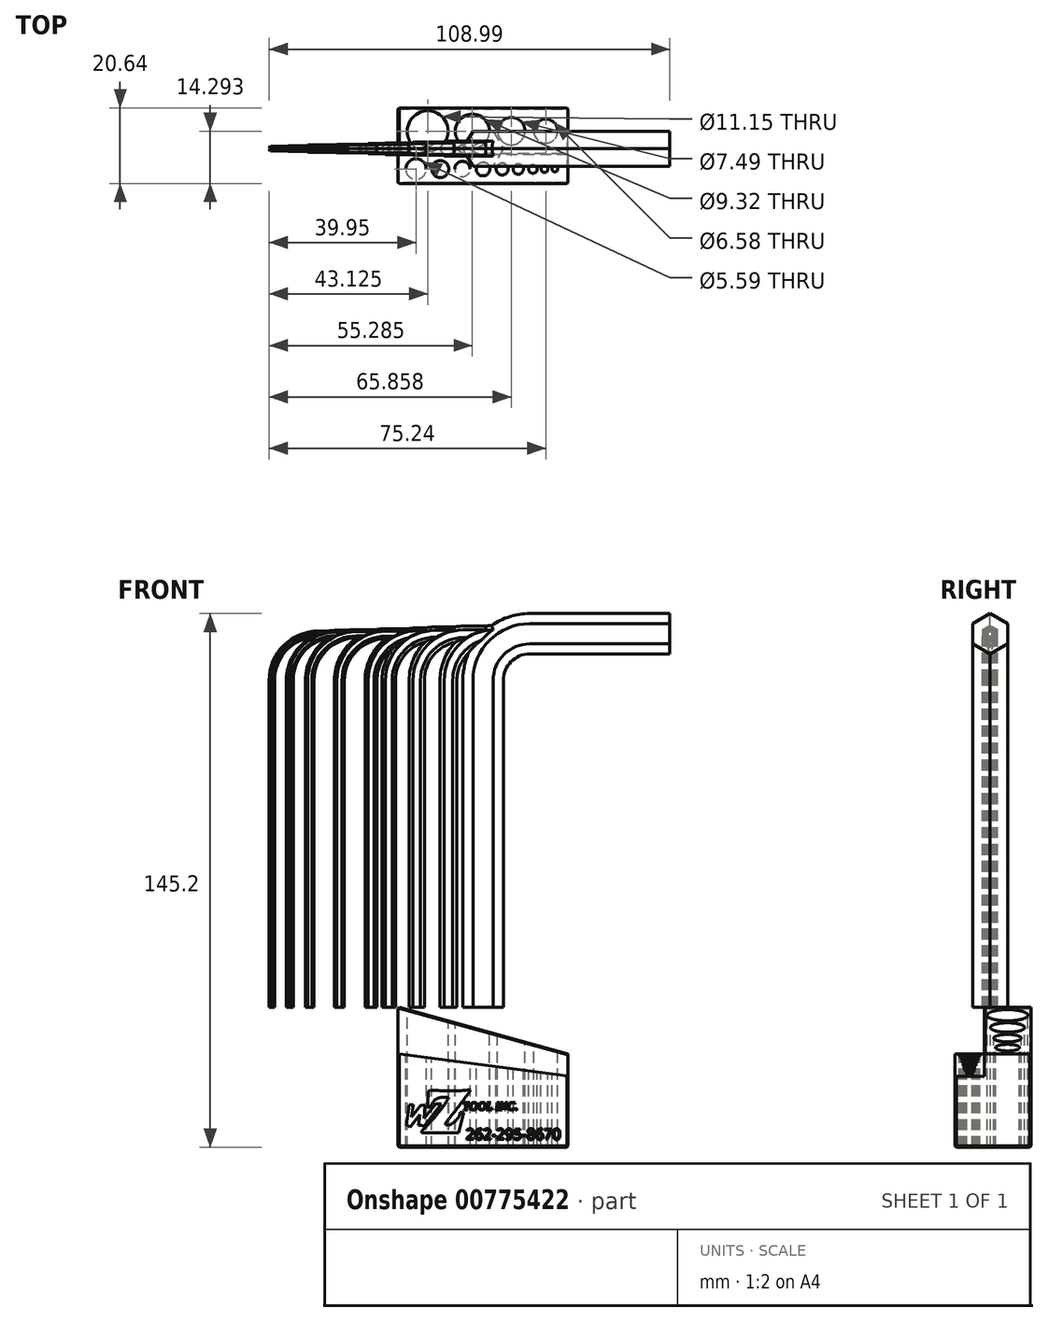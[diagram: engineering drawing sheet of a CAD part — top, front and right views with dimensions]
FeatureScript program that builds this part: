
annotation { "Feature Type Name" : "Feature", "Feature Type Description" : "" }
export const myFeature = defineFeature(function(context is Context, id is Id, definition is map)
    precondition{}
    {
        {
            var Q0;
            Q0=qCreatedBy(makeId("Top.planeOp"),FACE);
            var sketch = newSketch(context, id + "F0", { "sketchPlane" : qUnion([Q0])});
            skCircle(sketch, "E0.cCircle", {"center": v(0, 0) * mm, "radius": 4.76 * mm, "construction": true});
            skLineSegment(sketch, "E0.0", {"start": v(5.5, 0) * mm, "end": v(2.75, -4.76) * mm});
            skLineSegment(sketch, "E0.1", {"start": v(2.75, -4.76) * mm, "end": v(-2.75, -4.76) * mm});
            skLineSegment(sketch, "E0.2", {"start": v(-2.75, -4.76) * mm, "end": v(-5.5, 0) * mm});
            skLineSegment(sketch, "E0.3", {"start": v(-5.5, 0) * mm, "end": v(-2.75, 4.76) * mm});
            skLineSegment(sketch, "E0.4", {"start": v(-2.75, 4.76) * mm, "end": v(2.75, 4.76) * mm});
            skLineSegment(sketch, "E0.5", {"start": v(2.75, 4.76) * mm, "end": v(5.5, 0) * mm});
            skSolve(sketch);
        }
        {
            var Q0;
            Q0=qCreatedBy(makeId("Front.planeOp"),FACE);
            var sketch = newSketch(context, id + "F1", { "sketchPlane" : qUnion([Q0])});
            skPoint(sketch, "E1.0", {"position": v(0, 0) * mm});
            skLineSegment(sketch, "E2", {"start": v(0, 0) * mm, "end": v(0, 88.9) * mm});
            skLineSegment(sketch, "E3", {"start": v(12.7, 101.6) * mm, "end": v(50.8, 101.6) * mm});
            skPoint(sketch, "E4.visualSharp", {"position": v(0, 101.6) * mm});
            skArc(sketch, "E4.filletArc", {"start": v(12.7, 101.6) * mm, "mid": v(3.72, 97.88) * mm, "end": v(0, 88.9) * mm});
            skSolve(sketch);
        }
        {
            var Q0;
            Q0=makeQuery(id+"F0.imprint","IMPRINT",FACE,{"disambiguationData":[TD([[makeQuery(id+"F0.imprint","IMPRINT",EDGE,{"derivedFrom":sQuery(id+"F0.wireOp",EDGE,"E0.0")}),-1.0]])]});
            var Q1;
            Q1=sQuery(id+"F1.wireOp",EDGE,"E2");
            var Q2;
            Q2=sQuery(id+"F1.wireOp",EDGE,"E4.filletArc");
            var Q3;
            Q3=sQuery(id+"F1.wireOp",EDGE,"E3");
            sweep(context, id + "F2", {"profiles" : qUnion([Q0]), "path" : qUnion([Q1, Q2, Q3])});
        }
        {
            var Q0;
            Q0=qCreatedBy(makeId("Top.planeOp"),FACE);
            var sketch = newSketch(context, id + "F3", { "sketchPlane" : qUnion([Q0])});
            skCircle(sketch, "E5.cCircle", {"center": v(0, 0) * mm, "radius": 3.97 * mm, "construction": true});
            skLineSegment(sketch, "E5.0", {"start": v(4.58, 0) * mm, "end": v(2.3, -3.97) * mm});
            skLineSegment(sketch, "E5.1", {"start": v(2.3, -3.97) * mm, "end": v(-2.3, -3.97) * mm});
            skLineSegment(sketch, "E5.2", {"start": v(-2.3, -3.97) * mm, "end": v(-4.58, 0) * mm});
            skLineSegment(sketch, "E5.3", {"start": v(-4.58, 0) * mm, "end": v(-2.3, 3.97) * mm});
            skLineSegment(sketch, "E5.4", {"start": v(-2.3, 3.97) * mm, "end": v(2.3, 3.97) * mm});
            skLineSegment(sketch, "E5.5", {"start": v(2.3, 3.97) * mm, "end": v(4.58, 0) * mm});
            skSolve(sketch);
        }
        {
            var Q0;
            Q0 = qSketchRegion(id + "F3", true);
            var Q1;
            Q1=sQuery(id+"F1.wireOp",EDGE,"E2");
            var Q2;
            Q2=sQuery(id+"F1.wireOp",EDGE,"E4.filletArc");
            var Q3;
            Q3=sQuery(id+"F1.wireOp",EDGE,"E3");
            sweep(context, id + "F4", {"profiles" : qUnion([Q0]), "path" : qUnion([Q1, Q2, Q3])});
        }
        {
            var Q0;
            Q0=qCreatedBy(makeId("Top.planeOp"),FACE);
            var sketch = newSketch(context, id + "F5", { "sketchPlane" : qUnion([Q0])});
            skCircle(sketch, "E6.cCircle", {"center": v(0, 0) * mm, "radius": 3.18 * mm, "construction": true});
            skLineSegment(sketch, "E6.0", {"start": v(3.67, 0) * mm, "end": v(1.83, -3.17) * mm});
            skLineSegment(sketch, "E6.1", {"start": v(1.83, -3.17) * mm, "end": v(-1.83, -3.17) * mm});
            skLineSegment(sketch, "E6.2", {"start": v(-1.83, -3.17) * mm, "end": v(-3.67, 0) * mm});
            skLineSegment(sketch, "E6.3", {"start": v(-3.67, 0) * mm, "end": v(-1.83, 3.17) * mm});
            skLineSegment(sketch, "E6.4", {"start": v(-1.83, 3.17) * mm, "end": v(1.83, 3.17) * mm});
            skLineSegment(sketch, "E6.5", {"start": v(1.83, 3.17) * mm, "end": v(3.67, 0) * mm});
            skSolve(sketch);
        }
        {
            var Q0;
            Q0 = qSketchRegion(id + "F5", true);
            var Q1;
            Q1=sQuery(id+"F1.wireOp",EDGE,"E2");
            var Q2;
            Q2=sQuery(id+"F1.wireOp",EDGE,"E4.filletArc");
            var Q3;
            Q3=sQuery(id+"F1.wireOp",EDGE,"E3");
            sweep(context, id + "F6", {"profiles" : qUnion([Q0]), "path" : qUnion([Q1, Q2, Q3])});
        }
        {
            var Q0;
            Q0=qCreatedBy(makeId("Top.planeOp"),FACE);
            var sketch = newSketch(context, id + "F7", { "sketchPlane" : qUnion([Q0])});
            skCircle(sketch, "E7.cCircle", {"center": v(0, 0) * mm, "radius": 2.78 * mm, "construction": true});
            skLineSegment(sketch, "E7.0", {"start": v(3.2, 0) * mm, "end": v(1.6, -2.78) * mm});
            skLineSegment(sketch, "E7.1", {"start": v(1.6, -2.78) * mm, "end": v(-1.6, -2.78) * mm});
            skLineSegment(sketch, "E7.2", {"start": v(-1.6, -2.78) * mm, "end": v(-3.2, 0) * mm});
            skLineSegment(sketch, "E7.3", {"start": v(-3.2, 0) * mm, "end": v(-1.6, 2.78) * mm});
            skLineSegment(sketch, "E7.4", {"start": v(-1.6, 2.78) * mm, "end": v(1.6, 2.78) * mm});
            skLineSegment(sketch, "E7.5", {"start": v(1.6, 2.78) * mm, "end": v(3.2, 0) * mm});
            skSolve(sketch);
        }
        {
            var Q0;
            Q0=makeQuery(id+"F7.imprint","IMPRINT",FACE,{"disambiguationData":[TD([[makeQuery(id+"F7.imprint","IMPRINT",EDGE,{"derivedFrom":sQuery(id+"F7.wireOp",EDGE,"E7.0")}),-1.0]])]});
            var Q1;
            Q1=sQuery(id+"F1.wireOp",EDGE,"E2");
            var Q2;
            Q2=sQuery(id+"F1.wireOp",EDGE,"E4.filletArc");
            var Q3;
            Q3=sQuery(id+"F1.wireOp",EDGE,"E3");
            sweep(context, id + "F8", {"profiles" : qUnion([Q0]), "path" : qUnion([Q1, Q2, Q3])});
        }
        {
            var Q0;
            Q0=qCreatedBy(makeId("Top.planeOp"),FACE);
            var sketch = newSketch(context, id + "F9", { "sketchPlane" : qUnion([Q0])});
            skCircle(sketch, "E8.cCircle", {"center": v(0, 0) * mm, "radius": 2.38 * mm, "construction": true});
            skLineSegment(sketch, "E8.0", {"start": v(2.75, 0) * mm, "end": v(1.37, -2.38) * mm});
            skLineSegment(sketch, "E8.1", {"start": v(1.37, -2.38) * mm, "end": v(-1.37, -2.38) * mm});
            skLineSegment(sketch, "E8.2", {"start": v(-1.37, -2.38) * mm, "end": v(-2.75, 0) * mm});
            skLineSegment(sketch, "E8.3", {"start": v(-2.75, 0) * mm, "end": v(-1.37, 2.38) * mm});
            skLineSegment(sketch, "E8.4", {"start": v(-1.37, 2.38) * mm, "end": v(1.37, 2.38) * mm});
            skLineSegment(sketch, "E8.5", {"start": v(1.37, 2.38) * mm, "end": v(2.75, 0) * mm});
            skSolve(sketch);
        }
        {
            var Q0;
            Q0 = qSketchRegion(id + "F9", true);
            var Q1;
            Q1=sQuery(id+"F1.wireOp",EDGE,"E2");
            var Q2;
            Q2=sQuery(id+"F1.wireOp",EDGE,"E4.filletArc");
            var Q3;
            Q3=sQuery(id+"F1.wireOp",EDGE,"E3");
            sweep(context, id + "F10", {"profiles" : qUnion([Q0]), "path" : qUnion([Q1, Q2, Q3])});
        }
        {
            var Q0;
            Q0=qCreatedBy(makeId("Top.planeOp"),FACE);
            var sketch = newSketch(context, id + "F11", { "sketchPlane" : qUnion([Q0])});
            skCircle(sketch, "E9.cCircle", {"center": v(-47.15, 0) * mm, "radius": 1 * mm, "construction": true});
            skLineSegment(sketch, "E9.0", {"start": v(-46, 0) * mm, "end": v(-46.58, -1) * mm});
            skLineSegment(sketch, "E9.1", {"start": v(-46.58, -1) * mm, "end": v(-47.72, -1) * mm});
            skLineSegment(sketch, "E9.2", {"start": v(-47.72, -1) * mm, "end": v(-48.3, 0) * mm});
            skLineSegment(sketch, "E9.3", {"start": v(-48.3, 0) * mm, "end": v(-47.72, 1) * mm});
            skLineSegment(sketch, "E9.4", {"start": v(-47.72, 1) * mm, "end": v(-46.58, 1) * mm});
            skLineSegment(sketch, "E9.5", {"start": v(-46.58, 1) * mm, "end": v(-46, 0) * mm});
            skCircle(sketch, "E10.cCircle", {"center": v(-39.07, 0) * mm, "radius": 1.2 * mm, "construction": true});
            skLineSegment(sketch, "E10.0", {"start": v(-37.7, 0) * mm, "end": v(-38.39, -1.2) * mm});
            skLineSegment(sketch, "E10.1", {"start": v(-38.39, -1.2) * mm, "end": v(-39.76, -1.2) * mm});
            skLineSegment(sketch, "E10.2", {"start": v(-39.76, -1.2) * mm, "end": v(-40.45, 0) * mm});
            skLineSegment(sketch, "E10.3", {"start": v(-40.45, 0) * mm, "end": v(-39.76, 1.2) * mm});
            skLineSegment(sketch, "E10.4", {"start": v(-39.76, 1.2) * mm, "end": v(-38.39, 1.2) * mm});
            skLineSegment(sketch, "E10.5", {"start": v(-38.39, 1.2) * mm, "end": v(-37.7, 0) * mm});
            skCircle(sketch, "E11.cCircle", {"center": v(-52.58, 0) * mm, "radius": 0.8 * mm, "construction": true});
            skLineSegment(sketch, "E11.0", {"start": v(-51.66, 0) * mm, "end": v(-52.12, -0.8) * mm});
            skLineSegment(sketch, "E11.1", {"start": v(-52.12, -0.8) * mm, "end": v(-53.04, -0.8) * mm});
            skLineSegment(sketch, "E11.2", {"start": v(-53.04, -0.8) * mm, "end": v(-53.5, 0) * mm});
            skLineSegment(sketch, "E11.3", {"start": v(-53.5, 0) * mm, "end": v(-53.04, 0.8) * mm});
            skLineSegment(sketch, "E11.4", {"start": v(-53.04, 0.8) * mm, "end": v(-52.12, 0.8) * mm});
            skLineSegment(sketch, "E11.5", {"start": v(-52.12, 0.8) * mm, "end": v(-51.66, 0) * mm});
            skCircle(sketch, "E12.cCircle", {"center": v(-57.46, 0) * mm, "radius": 0.64 * mm, "construction": true});
            skLineSegment(sketch, "E12.0", {"start": v(-56.73, 0) * mm, "end": v(-57.1, -0.64) * mm});
            skLineSegment(sketch, "E12.1", {"start": v(-57.1, -0.63) * mm, "end": v(-57.83, -0.64) * mm});
            skLineSegment(sketch, "E12.2", {"start": v(-57.83, -0.63) * mm, "end": v(-58.2, 0) * mm});
            skLineSegment(sketch, "E12.3", {"start": v(-58.2, 0) * mm, "end": v(-57.83, 0.63) * mm});
            skLineSegment(sketch, "E12.4", {"start": v(-57.83, 0.63) * mm, "end": v(-57.1, 0.64) * mm});
            skLineSegment(sketch, "E12.5", {"start": v(-57.1, 0.64) * mm, "end": v(-56.73, 0) * mm});
            skCircle(sketch, "E13.cCircle", {"center": v(-9.42, 0) * mm, "radius": 1.98 * mm, "construction": true});
            skLineSegment(sketch, "E13.0", {"start": v(-7.12, 0) * mm, "end": v(-8.27, -1.98) * mm});
            skLineSegment(sketch, "E13.1", {"start": v(-8.27, -1.98) * mm, "end": v(-10.56, -1.98) * mm});
            skLineSegment(sketch, "E13.2", {"start": v(-10.56, -1.98) * mm, "end": v(-11.7, 0) * mm});
            skLineSegment(sketch, "E13.3", {"start": v(-11.7, 0) * mm, "end": v(-10.56, 1.98) * mm});
            skLineSegment(sketch, "E13.4", {"start": v(-10.56, 1.98) * mm, "end": v(-8.27, 1.98) * mm});
            skLineSegment(sketch, "E13.5", {"start": v(-8.27, 1.98) * mm, "end": v(-7.12, 0) * mm});
            skCircle(sketch, "E14.cCircle", {"center": v(-18.03, 0) * mm, "radius": 1.79 * mm, "construction": true});
            skLineSegment(sketch, "E14.0", {"start": v(-15.97, 0) * mm, "end": v(-17, -1.79) * mm});
            skLineSegment(sketch, "E14.1", {"start": v(-17, -1.79) * mm, "end": v(-19.07, -1.79) * mm});
            skLineSegment(sketch, "E14.2", {"start": v(-19.07, -1.79) * mm, "end": v(-20.1, 0) * mm});
            skLineSegment(sketch, "E14.3", {"start": v(-20.1, 0) * mm, "end": v(-19.07, 1.79) * mm});
            skLineSegment(sketch, "E14.4", {"start": v(-19.07, 1.79) * mm, "end": v(-17, 1.79) * mm});
            skLineSegment(sketch, "E14.5", {"start": v(-17, 1.79) * mm, "end": v(-15.97, 0) * mm});
            skCircle(sketch, "E15.cCircle", {"center": v(-25.65, 0) * mm, "radius": 1.59 * mm, "construction": true});
            skLineSegment(sketch, "E15.0", {"start": v(-23.82, 0) * mm, "end": v(-24.74, -1.59) * mm});
            skLineSegment(sketch, "E15.1", {"start": v(-24.74, -1.59) * mm, "end": v(-26.57, -1.59) * mm});
            skLineSegment(sketch, "E15.2", {"start": v(-26.57, -1.59) * mm, "end": v(-27.49, 0) * mm});
            skLineSegment(sketch, "E15.3", {"start": v(-27.49, 0) * mm, "end": v(-26.57, 1.59) * mm});
            skLineSegment(sketch, "E15.4", {"start": v(-26.57, 1.59) * mm, "end": v(-24.74, 1.59) * mm});
            skLineSegment(sketch, "E15.5", {"start": v(-24.74, 1.59) * mm, "end": v(-23.82, 0) * mm});
            skCircle(sketch, "E16.cCircle", {"center": v(-30.47, 0) * mm, "radius": 1.39 * mm, "construction": true});
            skLineSegment(sketch, "E16.0", {"start": v(-28.87, 0) * mm, "end": v(-29.67, -1.39) * mm});
            skLineSegment(sketch, "E16.1", {"start": v(-29.67, -1.39) * mm, "end": v(-31.28, -1.39) * mm});
            skLineSegment(sketch, "E16.2", {"start": v(-31.28, -1.39) * mm, "end": v(-32.08, 0) * mm});
            skLineSegment(sketch, "E16.3", {"start": v(-32.08, 0) * mm, "end": v(-31.28, 1.39) * mm});
            skLineSegment(sketch, "E16.4", {"start": v(-31.28, 1.39) * mm, "end": v(-29.67, 1.39) * mm});
            skLineSegment(sketch, "E16.5", {"start": v(-29.67, 1.39) * mm, "end": v(-28.87, 0) * mm});
            skSolve(sketch);
        }
        {
            var Q0;
            Q0=qCreatedBy(makeId("Front.planeOp"),FACE);
            var sketch = newSketch(context, id + "F12", { "sketchPlane" : qUnion([Q0])});
            skPoint(sketch, "E17.0", {"position": v(-9.42, 0) * mm});
            skLineSegment(sketch, "E18", {"start": v(-9.42, 0) * mm, "end": v(-9.42, 88.9) * mm});
            skLineSegment(sketch, "E19", {"start": v(3.28, 101.6) * mm, "end": v(41.38, 101.6) * mm});
            skPoint(sketch, "E20.visualSharp", {"position": v(-9.42, 101.6) * mm});
            skArc(sketch, "E20.filletArc", {"start": v(3.28, 101.6) * mm, "mid": v(-5.7, 97.88) * mm, "end": v(-9.42, 88.9) * mm});
            skPoint(sketch, "E21.0", {"position": v(-57.46, 0) * mm});
            skPoint(sketch, "E22.0", {"position": v(-52.58, 0) * mm});
            skPoint(sketch, "E23.0", {"position": v(-47.15, 0) * mm});
            skPoint(sketch, "E24.0", {"position": v(-39.07, 0) * mm});
            skPoint(sketch, "E25.0", {"position": v(-30.47, 0) * mm});
            skPoint(sketch, "E26.0", {"position": v(-25.65, 0) * mm});
            skPoint(sketch, "E27.0", {"position": v(-18.03, 0) * mm});
            skLineSegment(sketch, "E28", {"start": v(-18.03, 0) * mm, "end": v(-18.03, 88.9) * mm});
            skLineSegment(sketch, "E29", {"start": v(-5.33, 101.6) * mm, "end": v(32.77, 101.6) * mm});
            skPoint(sketch, "E30.visualSharp", {"position": v(-18.03, 101.6) * mm});
            skArc(sketch, "E30.filletArc", {"start": v(-5.33, 101.6) * mm, "mid": v(-14.31, 97.88) * mm, "end": v(-18.03, 88.9) * mm});
            skLineSegment(sketch, "E31", {"start": v(-25.65, 0) * mm, "end": v(-25.65, 88.9) * mm});
            skLineSegment(sketch, "E32", {"start": v(-12.95, 101.6) * mm, "end": v(25.15, 101.6) * mm});
            skPoint(sketch, "E33.visualSharp", {"position": v(-25.65, 101.6) * mm});
            skArc(sketch, "E33.filletArc", {"start": v(-12.95, 101.6) * mm, "mid": v(-21.93, 97.88) * mm, "end": v(-25.65, 88.9) * mm});
            skLineSegment(sketch, "E34", {"start": v(-39.07, 0) * mm, "end": v(-39.07, 88.9) * mm});
            skLineSegment(sketch, "E35", {"start": v(-26.37, 101.6) * mm, "end": v(11.73, 101.6) * mm});
            skPoint(sketch, "E36.visualSharp", {"position": v(-39.07, 101.6) * mm});
            skArc(sketch, "E36.filletArc", {"start": v(-26.37, 101.6) * mm, "mid": v(-35.35, 97.88) * mm, "end": v(-39.07, 88.9) * mm});
            skLineSegment(sketch, "E37", {"start": v(-47.15, 0) * mm, "end": v(-47.15, 88.9) * mm});
            skLineSegment(sketch, "E38", {"start": v(-34.45, 101.6) * mm, "end": v(3.65, 101.6) * mm});
            skPoint(sketch, "E39.visualSharp", {"position": v(-47.15, 101.6) * mm});
            skArc(sketch, "E39.filletArc", {"start": v(-34.45, 101.6) * mm, "mid": v(-43.43, 97.88) * mm, "end": v(-47.15, 88.9) * mm});
            skLineSegment(sketch, "E40", {"start": v(-52.58, 0) * mm, "end": v(-52.58, 88.9) * mm});
            skLineSegment(sketch, "E41", {"start": v(-39.88, 101.6) * mm, "end": v(-1.78, 101.6) * mm});
            skPoint(sketch, "E42.visualSharp", {"position": v(-52.58, 101.6) * mm});
            skArc(sketch, "E42.filletArc", {"start": v(-39.88, 101.6) * mm, "mid": v(-48.86, 97.88) * mm, "end": v(-52.58, 88.9) * mm});
            skLineSegment(sketch, "E43", {"start": v(-57.46, 0) * mm, "end": v(-57.46, 88.9) * mm});
            skLineSegment(sketch, "E44", {"start": v(-44.76, 101.6) * mm, "end": v(-6.66, 101.6) * mm});
            skPoint(sketch, "E45.visualSharp", {"position": v(-57.46, 101.6) * mm});
            skArc(sketch, "E45.filletArc", {"start": v(-44.76, 101.6) * mm, "mid": v(-53.74, 97.88) * mm, "end": v(-57.46, 88.9) * mm});
            skLineSegment(sketch, "E46", {"start": v(-30.47, 0) * mm, "end": v(-30.47, 88.9) * mm});
            skLineSegment(sketch, "E47", {"start": v(-17.77, 101.6) * mm, "end": v(20.33, 101.6) * mm});
            skPoint(sketch, "E48.visualSharp", {"position": v(-30.47, 101.6) * mm});
            skArc(sketch, "E48.filletArc", {"start": v(-17.77, 101.6) * mm, "mid": v(-26.75, 97.88) * mm, "end": v(-30.47, 88.9) * mm});
            skLineSegment(sketch, "E49", {"start": v(-12.95, 101.6) * mm, "end": v(11.73, 101.6) * mm});
            skSolve(sketch);
        }
        {
            var Q0;
            Q0=makeQuery(id+"F11.imprint","IMPRINT",FACE,{"disambiguationData":[TD([[makeQuery(id+"F11.imprint","IMPRINT",EDGE,{"derivedFrom":sQuery(id+"F11.wireOp",EDGE,"E13.0")}),-1.0]])]});
            var Q1;
            Q1=makeQuery(id+"F11.imprint","IMPRINT",FACE,{"disambiguationData":[TD([[makeQuery(id+"F11.imprint","IMPRINT",EDGE,{"derivedFrom":sQuery(id+"F11.wireOp",EDGE,"E14.0")}),-1.0]])]});
            var Q2;
            Q2=makeQuery(id+"F11.imprint","IMPRINT",FACE,{"disambiguationData":[TD([[makeQuery(id+"F11.imprint","IMPRINT",EDGE,{"derivedFrom":sQuery(id+"F11.wireOp",EDGE,"E15.0")}),-1.0]])]});
            var Q3;
            Q3=makeQuery(id+"F11.imprint","IMPRINT",FACE,{"disambiguationData":[TD([[makeQuery(id+"F11.imprint","IMPRINT",EDGE,{"derivedFrom":sQuery(id+"F11.wireOp",EDGE,"E16.0")}),-1.0]])]});
            var Q4;
            Q4=makeQuery(id+"F11.imprint","IMPRINT",FACE,{"disambiguationData":[TD([[makeQuery(id+"F11.imprint","IMPRINT",EDGE,{"derivedFrom":sQuery(id+"F11.wireOp",EDGE,"E10.0")}),-1.0]])]});
            var Q5;
            Q5=makeQuery(id+"F11.imprint","IMPRINT",FACE,{"disambiguationData":[TD([[makeQuery(id+"F11.imprint","IMPRINT",EDGE,{"derivedFrom":sQuery(id+"F11.wireOp",EDGE,"E9.0")}),-1.0]])]});
            var Q6;
            Q6=makeQuery(id+"F11.imprint","IMPRINT",FACE,{"disambiguationData":[TD([[makeQuery(id+"F11.imprint","IMPRINT",EDGE,{"derivedFrom":sQuery(id+"F11.wireOp",EDGE,"E11.0")}),-1.0]])]});
            var Q7;
            Q7=makeQuery(id+"F11.imprint","IMPRINT",FACE,{"disambiguationData":[TD([[makeQuery(id+"F11.imprint","IMPRINT",EDGE,{"derivedFrom":sQuery(id+"F11.wireOp",EDGE,"E12.0")}),-1.0]])]});
            var Q8;
            Q8=sQuery(id+"F12.wireOp",EDGE,"E18");
            sweep(context, id + "F13", {"profiles" : qUnion([Q0, Q1, Q2, Q3, Q4, Q5, Q6, Q7]), "path" : qUnion([Q8])});
        }
        {
            var Q0;
            Q0=makeQuery(id+"F13.opSweep","CAP_FACE",FACE,{"disambiguationData":[OSD([sQuery(id+"F11.wireOp",EDGE,"E13.0"),sQuery(id+"F11.wireOp",EDGE,"E13.1"),sQuery(id+"F11.wireOp",EDGE,"E13.2"),sQuery(id+"F11.wireOp",EDGE,"E13.3"),sQuery(id+"F11.wireOp",EDGE,"E13.4"),sQuery(id+"F11.wireOp",EDGE,"E13.5"),sQuery(id+"F12.wireOp",VERTEX,"E18.end")])],"isStart":false});
            var Q1;
            Q1=makeQuery(id+"F13.opSweep","CAP_EDGE",EDGE,{"disambiguationData":[OSD([sQuery(id+"F11.wireOp",EDGE,"E13.1"),sQuery(id+"F12.wireOp",VERTEX,"E18.end")])],"isStart":false});
            var Q2;
            Q2=makeQuery(id+"F13.opSweep","CAP_EDGE",EDGE,{"disambiguationData":[OSD([sQuery(id+"F11.wireOp",EDGE,"E13.0"),sQuery(id+"F12.wireOp",VERTEX,"E18.end")])],"isStart":false});
            var Q3;
            Q3=makeQuery(id+"F13.opSweep","CAP_EDGE",EDGE,{"disambiguationData":[OSD([sQuery(id+"F11.wireOp",EDGE,"E13.5"),sQuery(id+"F12.wireOp",VERTEX,"E18.end")])],"isStart":false});
            var Q4;
            Q4=makeQuery(id+"F13.opSweep","CAP_EDGE",EDGE,{"disambiguationData":[OSD([sQuery(id+"F11.wireOp",EDGE,"E13.4"),sQuery(id+"F12.wireOp",VERTEX,"E18.end")])],"isStart":false});
            var Q5;
            Q5=sQuery(id+"F12.wireOp",EDGE,"E20.filletArc");
            var Q6;
            Q6=sQuery(id+"F12.wireOp",EDGE,"E19");
            sweep(context, id + "F14", {"operationType" : NewBodyOperationType.ADD, "profiles" : qUnion([Q0]), "surfaceProfiles" : qUnion([Q1, Q2, Q3, Q4]), "path" : qUnion([Q5, Q6])});
        }
        {
            var Q0;
            Q0=makeQuery(id+"F13.opSweep","CAP_FACE",FACE,{"disambiguationData":[OSD([sQuery(id+"F11.wireOp",EDGE,"E14.0"),sQuery(id+"F11.wireOp",EDGE,"E14.1"),sQuery(id+"F11.wireOp",EDGE,"E14.2"),sQuery(id+"F11.wireOp",EDGE,"E14.3"),sQuery(id+"F11.wireOp",EDGE,"E14.4"),sQuery(id+"F11.wireOp",EDGE,"E14.5"),sQuery(id+"F12.wireOp",VERTEX,"E18.end")])],"isStart":false});
            var Q1;
            Q1=sQuery(id+"F12.wireOp",EDGE,"E30.filletArc");
            var Q2;
            Q2=sQuery(id+"F12.wireOp",EDGE,"E29");
            sweep(context, id + "F15", {"operationType" : NewBodyOperationType.ADD, "profiles" : qUnion([Q0]), "path" : qUnion([Q1, Q2])});
        }
        {
            var Q0;
            Q0=makeQuery(id+"F13.opSweep","CAP_FACE",FACE,{"disambiguationData":[OSD([sQuery(id+"F11.wireOp",EDGE,"E15.0"),sQuery(id+"F11.wireOp",EDGE,"E15.1"),sQuery(id+"F11.wireOp",EDGE,"E15.2"),sQuery(id+"F11.wireOp",EDGE,"E15.3"),sQuery(id+"F11.wireOp",EDGE,"E15.4"),sQuery(id+"F11.wireOp",EDGE,"E15.5"),sQuery(id+"F12.wireOp",VERTEX,"E18.end")])],"isStart":false});
            var Q1;
            Q1=sQuery(id+"F12.wireOp",EDGE,"E33.filletArc");
            sweep(context, id + "F16", {"operationType" : NewBodyOperationType.ADD, "profiles" : qUnion([Q0]), "path" : qUnion([Q1])});
        }
        {
            var Q0;
            Q0=makeQuery(id+"F13.opSweep","CAP_FACE",FACE,{"disambiguationData":[OSD([sQuery(id+"F11.wireOp",EDGE,"E16.0"),sQuery(id+"F11.wireOp",EDGE,"E16.1"),sQuery(id+"F11.wireOp",EDGE,"E16.2"),sQuery(id+"F11.wireOp",EDGE,"E16.3"),sQuery(id+"F11.wireOp",EDGE,"E16.4"),sQuery(id+"F11.wireOp",EDGE,"E16.5"),sQuery(id+"F12.wireOp",VERTEX,"E18.end")])],"isStart":false});
            var Q1;
            Q1=sQuery(id+"F12.wireOp",EDGE,"E48.filletArc");
            sweep(context, id + "F17", {"operationType" : NewBodyOperationType.ADD, "profiles" : qUnion([Q0]), "path" : qUnion([Q1])});
        }
        {
            var Q0;
            Q0=makeQuery(id+"F13.opSweep","CAP_FACE",FACE,{"disambiguationData":[OSD([sQuery(id+"F11.wireOp",EDGE,"E10.0"),sQuery(id+"F11.wireOp",EDGE,"E10.1"),sQuery(id+"F11.wireOp",EDGE,"E10.2"),sQuery(id+"F11.wireOp",EDGE,"E10.3"),sQuery(id+"F11.wireOp",EDGE,"E10.4"),sQuery(id+"F11.wireOp",EDGE,"E10.5"),sQuery(id+"F12.wireOp",VERTEX,"E18.end")])],"isStart":false});
            var Q1;
            Q1=sQuery(id+"F12.wireOp",EDGE,"E36.filletArc");
            sweep(context, id + "F18", {"operationType" : NewBodyOperationType.ADD, "profiles" : qUnion([Q0]), "path" : qUnion([Q1])});
        }
        {
            var Q0;
            Q0=makeQuery(id+"F13.opSweep","CAP_FACE",FACE,{"disambiguationData":[OSD([sQuery(id+"F11.wireOp",EDGE,"E9.0"),sQuery(id+"F11.wireOp",EDGE,"E9.1"),sQuery(id+"F11.wireOp",EDGE,"E9.2"),sQuery(id+"F11.wireOp",EDGE,"E9.3"),sQuery(id+"F11.wireOp",EDGE,"E9.4"),sQuery(id+"F11.wireOp",EDGE,"E9.5"),sQuery(id+"F12.wireOp",VERTEX,"E18.end")])],"isStart":false});
            var Q1;
            Q1=sQuery(id+"F12.wireOp",EDGE,"E39.filletArc");
            sweep(context, id + "F19", {"operationType" : NewBodyOperationType.ADD, "profiles" : qUnion([Q0]), "path" : qUnion([Q1])});
        }
        {
            var Q0;
            Q0=makeQuery(id+"F13.opSweep","CAP_FACE",FACE,{"disambiguationData":[OSD([sQuery(id+"F11.wireOp",EDGE,"E11.0"),sQuery(id+"F11.wireOp",EDGE,"E11.1"),sQuery(id+"F11.wireOp",EDGE,"E11.2"),sQuery(id+"F11.wireOp",EDGE,"E11.3"),sQuery(id+"F11.wireOp",EDGE,"E11.4"),sQuery(id+"F11.wireOp",EDGE,"E11.5"),sQuery(id+"F12.wireOp",VERTEX,"E18.end")])],"isStart":false});
            var Q1;
            Q1=sQuery(id+"F12.wireOp",EDGE,"E42.filletArc");
            sweep(context, id + "F20", {"operationType" : NewBodyOperationType.ADD, "profiles" : qUnion([Q0]), "path" : qUnion([Q1])});
        }
        {
            var Q0;
            Q0=makeQuery(id+"F13.opSweep","CAP_FACE",FACE,{"disambiguationData":[OSD([sQuery(id+"F11.wireOp",EDGE,"E12.0"),sQuery(id+"F11.wireOp",EDGE,"E12.1"),sQuery(id+"F11.wireOp",EDGE,"E12.2"),sQuery(id+"F11.wireOp",EDGE,"E12.3"),sQuery(id+"F11.wireOp",EDGE,"E12.4"),sQuery(id+"F11.wireOp",EDGE,"E12.5"),sQuery(id+"F12.wireOp",VERTEX,"E18.end")])],"isStart":false});
            var Q1;
            Q1=sQuery(id+"F12.wireOp",EDGE,"E45.filletArc");
            sweep(context, id + "F21", {"operationType" : NewBodyOperationType.ADD, "profiles" : qUnion([Q0]), "path" : qUnion([Q1])});
        }
        {
            var Q0;
            Q0=qCreatedBy(makeId("Front.planeOp"),FACE);
            var sketch = newSketch(context, id + "F22", { "sketchPlane" : qUnion([Q0])});
            skPoint(sketch, "E50.0", {"position": v(-12.95, 101.6) * mm});
            skLineSegment(sketch, "E51", {"start": v(-12.95, 101.6) * mm, "end": v(25.15, 101.6) * mm});
            skSolve(sketch);
        }
        {
            var Q0;
            Q0=makeQuery(id+"F16.opSweep","CAP_FACE",FACE,{"disambiguationData":[OSD([sQuery(id+"F11.wireOp",EDGE,"E15.0"),sQuery(id+"F11.wireOp",EDGE,"E15.1"),sQuery(id+"F11.wireOp",EDGE,"E15.2"),sQuery(id+"F11.wireOp",EDGE,"E15.3"),sQuery(id+"F11.wireOp",EDGE,"E15.4"),sQuery(id+"F11.wireOp",EDGE,"E15.5"),sQuery(id+"F12.wireOp",VERTEX,"E18.end"),sQuery(id+"F12.wireOp",VERTEX,"E33.filletArc.start")])],"isStart":false});
            var Q1;
            Q1=sQuery(id+"F22.wireOp",EDGE,"E51");
            sweep(context, id + "F23", {"operationType" : NewBodyOperationType.ADD, "profiles" : qUnion([Q0]), "path" : qUnion([Q1])});
        }
        {
            var Q0;
            Q0=qCreatedBy(makeId("Front.planeOp"),FACE);
            var sketch = newSketch(context, id + "F24", { "sketchPlane" : qUnion([Q0])});
            skPoint(sketch, "E52.0", {"position": v(-17.77, 101.6) * mm});
            skLineSegment(sketch, "E53", {"start": v(-17.77, 101.6) * mm, "end": v(20.33, 101.6) * mm});
            skSolve(sketch);
        }
        {
            var Q0;
            Q0=makeQuery(id+"F17.opSweep","CAP_FACE",FACE,{"disambiguationData":[OSD([sQuery(id+"F11.wireOp",EDGE,"E16.0"),sQuery(id+"F11.wireOp",EDGE,"E16.1"),sQuery(id+"F11.wireOp",EDGE,"E16.2"),sQuery(id+"F11.wireOp",EDGE,"E16.3"),sQuery(id+"F11.wireOp",EDGE,"E16.4"),sQuery(id+"F11.wireOp",EDGE,"E16.5"),sQuery(id+"F12.wireOp",VERTEX,"E18.end"),sQuery(id+"F12.wireOp",VERTEX,"E48.filletArc.start")])],"isStart":false});
            var Q1;
            Q1=sQuery(id+"F24.wireOp",EDGE,"E53");
            sweep(context, id + "F25", {"operationType" : NewBodyOperationType.ADD, "profiles" : qUnion([Q0]), "path" : qUnion([Q1])});
        }
        {
            var Q0;
            Q0=qCreatedBy(makeId("Front.planeOp"),FACE);
            var sketch = newSketch(context, id + "F26", { "sketchPlane" : qUnion([Q0])});
            skPoint(sketch, "E54.0", {"position": v(-26.37, 101.6) * mm});
            skLineSegment(sketch, "E55", {"start": v(-26.37, 101.6) * mm, "end": v(11.73, 101.6) * mm});
            skSolve(sketch);
        }
        {
            var Q0;
            Q0=makeQuery(id+"F18.opSweep","CAP_FACE",FACE,{"disambiguationData":[OSD([sQuery(id+"F11.wireOp",EDGE,"E10.0"),sQuery(id+"F11.wireOp",EDGE,"E10.1"),sQuery(id+"F11.wireOp",EDGE,"E10.2"),sQuery(id+"F11.wireOp",EDGE,"E10.3"),sQuery(id+"F11.wireOp",EDGE,"E10.4"),sQuery(id+"F11.wireOp",EDGE,"E10.5"),sQuery(id+"F12.wireOp",VERTEX,"E18.end"),sQuery(id+"F12.wireOp",VERTEX,"E36.filletArc.start")])],"isStart":false});
            var Q1;
            Q1=sQuery(id+"F26.wireOp",EDGE,"E55");
            sweep(context, id + "F27", {"operationType" : NewBodyOperationType.ADD, "profiles" : qUnion([Q0]), "path" : qUnion([Q1])});
        }
        {
            var Q0;
            Q0=qCreatedBy(makeId("Front.planeOp"),FACE);
            var sketch = newSketch(context, id + "F28", { "sketchPlane" : qUnion([Q0])});
            skPoint(sketch, "E56.0", {"position": v(-34.45, 101.6) * mm});
            skPoint(sketch, "E57.0", {"position": v(-39.88, 101.6) * mm});
            skPoint(sketch, "E58.0", {"position": v(-44.76, 101.6) * mm});
            skLineSegment(sketch, "E59", {"start": v(-34.45, 101.6) * mm, "end": v(3.65, 101.6) * mm});
            skLineSegment(sketch, "E60", {"start": v(-39.88, 101.6) * mm, "end": v(-1.78, 101.6) * mm});
            skLineSegment(sketch, "E61", {"start": v(-44.76, 101.6) * mm, "end": v(-6.66, 101.6) * mm});
            skSolve(sketch);
        }
        {
            var Q0;
            Q0=makeQuery(id+"F19.opSweep","CAP_FACE",FACE,{"disambiguationData":[OSD([sQuery(id+"F11.wireOp",EDGE,"E9.0"),sQuery(id+"F11.wireOp",EDGE,"E9.1"),sQuery(id+"F11.wireOp",EDGE,"E9.2"),sQuery(id+"F11.wireOp",EDGE,"E9.3"),sQuery(id+"F11.wireOp",EDGE,"E9.4"),sQuery(id+"F11.wireOp",EDGE,"E9.5"),sQuery(id+"F12.wireOp",VERTEX,"E18.end"),sQuery(id+"F12.wireOp",VERTEX,"E39.filletArc.start")])],"isStart":false});
            var Q1;
            Q1=sQuery(id+"F28.wireOp",EDGE,"E59");
            sweep(context, id + "F29", {"operationType" : NewBodyOperationType.ADD, "profiles" : qUnion([Q0]), "path" : qUnion([Q1])});
        }
        {
            var Q0;
            Q0=makeQuery(id+"F20.opSweep","CAP_FACE",FACE,{"disambiguationData":[OSD([sQuery(id+"F11.wireOp",EDGE,"E11.0"),sQuery(id+"F11.wireOp",EDGE,"E11.1"),sQuery(id+"F11.wireOp",EDGE,"E11.2"),sQuery(id+"F11.wireOp",EDGE,"E11.3"),sQuery(id+"F11.wireOp",EDGE,"E11.4"),sQuery(id+"F11.wireOp",EDGE,"E11.5"),sQuery(id+"F12.wireOp",VERTEX,"E18.end"),sQuery(id+"F12.wireOp",VERTEX,"E42.filletArc.start")])],"isStart":false});
            var Q1;
            Q1=sQuery(id+"F28.wireOp",EDGE,"E60");
            sweep(context, id + "F30", {"operationType" : NewBodyOperationType.ADD, "profiles" : qUnion([Q0]), "path" : qUnion([Q1])});
        }
        {
            var Q0;
            Q0=makeQuery(id+"F21.opSweep","CAP_FACE",FACE,{"disambiguationData":[OSD([sQuery(id+"F11.wireOp",EDGE,"E12.0"),sQuery(id+"F11.wireOp",EDGE,"E12.1"),sQuery(id+"F11.wireOp",EDGE,"E12.2"),sQuery(id+"F11.wireOp",EDGE,"E12.3"),sQuery(id+"F11.wireOp",EDGE,"E12.4"),sQuery(id+"F11.wireOp",EDGE,"E12.5"),sQuery(id+"F12.wireOp",VERTEX,"E18.end"),sQuery(id+"F12.wireOp",VERTEX,"E45.filletArc.start")])],"isStart":false});
            var Q1;
            Q1=sQuery(id+"F28.wireOp",EDGE,"E61");
            sweep(context, id + "F31", {"operationType" : NewBodyOperationType.ADD, "profiles" : qUnion([Q0]), "path" : qUnion([Q1])});
        }
        {
            var Q0;
            Q0=qCreatedBy(makeId("Top.planeOp"),FACE);
            var sketch = newSketch(context, id + "F32", { "sketchPlane" : qUnion([Q0])});
            skLineSegment(sketch, "E62.top", {"start": v(23.13, 11.11) * mm, "end": v(-23.13, 11.11) * mm});
            skLineSegment(sketch, "E62.right", {"start": v(-23.13, -5.56) * mm, "end": v(-23.13, 11.11) * mm});
            skLineSegment(sketch, "E63", {"start": v(-23.13, -1.59) * mm, "end": v(23.13, -1.59) * mm});
            skLineSegment(sketch, "E64", {"start": v(-23.13, 11.11) * mm, "end": v(-23.13, -1.59) * mm, "construction": true});
            skLineSegment(sketch, "E65", {"start": v(-23.13, 4.76) * mm, "end": v(23.13, 4.76) * mm, "construction": true});
            skLineSegment(sketch, "E66", {"start": v(-23.13, -5.56) * mm, "end": v(23.13, -5.56) * mm, "construction": true});
            skCircle(sketch, "E67", {"center": v(-15.07, 4.76) * mm, "radius": 5.58 * mm});
            skCircle(sketch, "E68", {"center": v(7.67, 4.76) * mm, "radius": 3.75 * mm});
            skCircle(sketch, "E69", {"center": v(-2.9, 4.76) * mm, "radius": 4.66 * mm});
            skCircle(sketch, "E70", {"center": v(17.05, 4.76) * mm, "radius": 3.29 * mm});
            skCircle(sketch, "E71", {"center": v(-18.24, -5.56) * mm, "radius": 2.8 * mm});
            skCircle(sketch, "E72", {"center": v(5.2, -5.56) * mm, "radius": 1.64 * mm});
            skCircle(sketch, "E73", {"center": v(-0.02, -5.56) * mm, "radius": 1.87 * mm});
            skCircle(sketch, "E74", {"center": v(-5.63, -5.56) * mm, "radius": 2.1 * mm});
            skCircle(sketch, "E75", {"center": v(-11.64, -5.56) * mm, "radius": 2.32 * mm});
            skCircle(sketch, "E76", {"center": v(9.59, -5.56) * mm, "radius": 1.4 * mm});
            skCircle(sketch, "E77", {"center": v(13.55, -5.56) * mm, "radius": 1.18 * mm});
            skCircle(sketch, "E78", {"center": v(16.72, -5.56) * mm, "radius": 0.95 * mm});
            skCircle(sketch, "E79", {"center": v(19.53, -5.56) * mm, "radius": 0.77 * mm});
            skLineSegment(sketch, "E80", {"start": v(23.13, 11.11) * mm, "end": v(23.13, -5.56) * mm});
            skLineSegment(sketch, "E81", {"start": v(23.13, 0) * mm, "end": v(-23.13, 0) * mm, "construction": true});
            skLineSegment(sketch, "E82", {"start": v(-23.13, -5.56) * mm, "end": v(-23.13, -9.53) * mm});
            skLineSegment(sketch, "E83", {"start": v(-23.13, -9.53) * mm, "end": v(23.13, -9.52) * mm});
            skLineSegment(sketch, "E84", {"start": v(23.13, -9.52) * mm, "end": v(23.13, -5.56) * mm});
            skSolve(sketch);
        }
        {
            var Q0;
            {var subQ2=sQuery(id+"F32.wireOp",EDGE,"E62.top");Q0=makeQuery(id+"F32.imprint","IMPRINT",FACE,{"disambiguationData":[TD([[makeQuery(id+"F32.imprint","IMPRINT",EDGE,{"derivedFrom":subQ2}),1.0]])]});}
            var Q1;
            {var subQ2=sQuery(id+"F32.wireOp",EDGE,"E63");Q1=makeQuery(id+"F32.imprint","IMPRINT",FACE,{"disambiguationData":[TD([[makeQuery(id+"F32.imprint","IMPRINT",EDGE,{"derivedFrom":subQ2}),-1.0]])]});}
            extrude(context, id + "F33", {"entities" : qUnion([Q0, Q1]), "depth" : -38.1 * mm, "offsetDistance" : 25.4 * mm});
        }
        {
            var Q0;
            {var subQ2=sQuery(id+"F32.wireOp",EDGE,"E63");Q0=makeQuery(id+"F32.imprint","IMPRINT",FACE,{"disambiguationData":[TD([[makeQuery(id+"F32.imprint","IMPRINT",EDGE,{"derivedFrom":subQ2}),-1.0]])]});}
            extrude(context, id + "F34", {"entities" : qUnion([Q0]), "operationType" : NewBodyOperationType.REMOVE, "oppositeDirection" : true, "depth" : 12.7 * mm, "offsetDistance" : 25.4 * mm});
        }
        {
            var Q0;
            Q0=makeQuery(id+"F33.opExtrude","SWEPT_FACE",FACE,{"disambiguationData":[OSD([sQuery(id+"F32.wireOp",EDGE,"E62.top")])]});
            var sketch = newSketch(context, id + "F35", { "sketchPlane" : qUnion([Q0])});
            skLineSegment(sketch, "E85", {"start": v(23.13, 0) * mm, "end": v(-23.13, -12.7) * mm});
            skPoint(sketch, "E86.0", {"position": v(-23.13, -12.7) * mm});
            skSolve(sketch);
        }
        {
            var Q0;
            {var subQ0=sQuery(id+"F35.wireOp",EDGE,"E85");Q0=makeQuery(id+"F35.imprint","IMPRINT",FACE,{"disambiguationData":[TD([[makeQuery(id+"F35.imprint","IMPRINT",EDGE,{"derivedFrom":subQ0}),-1.0]])]});}
            extrude(context, id + "F36", {"entities" : qUnion([Q0]), "operationType" : NewBodyOperationType.REMOVE, "endBound" : BoundingType.THROUGH_ALL, "oppositeDirection" : true, "depth" : 25.4 * mm, "offsetDistance" : 25.4 * mm});
        }
        {
            var Q0;
            Q0=makeQuery(id+"F33.opExtrude","SWEPT_FACE",FACE,{"disambiguationData":[OSD([sQuery(id+"F32.wireOp",EDGE,"E83")])]});
            var sketch = newSketch(context, id + "F37", { "sketchPlane" : qUnion([Q0])});
            skLineSegment(sketch, "E87", {"start": v(-23.13, -12.7) * mm, "end": v(23.13, -18.8) * mm});
            skSolve(sketch);
        }
        {
            var Q0;
            {var subQ0=sQuery(id+"F37.wireOp",EDGE,"E87");Q0=makeQuery(id+"F37.imprint","IMPRINT",FACE,{"disambiguationData":[TD([[makeQuery(id+"F37.imprint","IMPRINT",EDGE,{"derivedFrom":subQ0}),1.0]])]});}
            var Q1;
            Q1=makeQuery(id+"F34.boolean.opBoolean","COPY",FACE,{"derivedFrom":makeQuery(id+"F34.opExtrude","SWEPT_FACE",FACE,{"disambiguationData":[OSD([sQuery(id+"F32.wireOp",EDGE,"E63")])]})});
            extrude(context, id + "F38", {"entities" : qUnion([Q0]), "operationType" : NewBodyOperationType.REMOVE, "endBound" : BoundingType.UP_TO_SURFACE, "oppositeDirection" : true, "depth" : 25.4 * mm, "endBoundEntityFace" : qUnion([Q1]), "offsetDistance" : 25.4 * mm});
        }
        {
            var Q0;
            Q0=makeQuery(id+"F33.opExtrude","SWEPT_FACE",FACE,{"disambiguationData":[OSD([sQuery(id+"F32.wireOp",EDGE,"E83")])]});
            var sketch = newSketch(context, id + "F39", { "sketchPlane" : qUnion([Q0])});
            skFitSpline(sketch, "E88", {"points": [v(-14.69, -22.72) * mm, v(-3.6, -22.47) * mm], "startDerivative": vector(11.3, 0.33) * mm, "endDerivative": vector(11.03, 1.76) * mm});
            skFitSpline(sketch, "E89", {"points": [v(-3.37, -22.47) * mm, v(-10, -31.24) * mm], "startDerivative": vector(-5.83, -9.12) * mm, "endDerivative": vector(-6.89, -8.9) * mm});
            skLineSegment(sketch, "E90", {"start": v(-3.6, -22.47) * mm, "end": v(-3.37, -22.47) * mm});
            skFitSpline(sketch, "E91", {"points": [v(-10, -31.24) * mm, v(-8.4, -31.72) * mm], "startDerivative": vector(-2.3, -4.17) * mm, "endDerivative": vector(1.18, 0.85) * mm});
            skFitSpline(sketch, "E92", {"points": [v(-8.4, -31.72) * mm, v(-6.27, -28.87) * mm], "startDerivative": vector(3.33, 2.27) * mm, "endDerivative": vector(0.09, 3) * mm});
            skLineSegment(sketch, "E93", {"start": v(-6.27, -28.87) * mm, "end": v(-6.27, -28.58) * mm});
            skLineSegment(sketch, "E94", {"start": v(-6.27, -28.58) * mm, "end": v(-5.27, -28.58) * mm});
            skLineSegment(sketch, "E95", {"start": v(-5.27, -28.58) * mm, "end": v(-6.63, -34.25) * mm});
            skLineSegment(sketch, "E96", {"start": v(-6.63, -34.25) * mm, "end": v(-16.74, -34.25) * mm});
            skLineSegment(sketch, "E97", {"start": v(-16.74, -34.25) * mm, "end": v(-16.74, -33.76) * mm});
            skFitSpline(sketch, "E98", {"points": [v(-16.74, -33.76) * mm, v(-9.37, -24.6) * mm], "startDerivative": vector(8.1, 8.5) * mm, "endDerivative": vector(5.05, 10.05) * mm});
            skLineSegment(sketch, "E99", {"start": v(-9.37, -24.6) * mm, "end": v(-11.58, -24.6) * mm});
            skFitSpline(sketch, "E100", {"points": [v(-11.58, -24.6) * mm, v(-14.4, -27.25) * mm], "startDerivative": vector(-3.35, -0.99) * mm, "endDerivative": vector(-3.8, -7.36) * mm});
            skLineSegment(sketch, "E101", {"start": v(-14.4, -27.25) * mm, "end": v(-15.11, -27.25) * mm});
            skLineSegment(sketch, "E102", {"start": v(-14.69, -22.72) * mm, "end": v(-14.89, -22.72) * mm});
            skFitSpline(sketch, "E103", {"points": [v(-14.89, -22.72) * mm, v(-15.11, -27.25) * mm], "startDerivative": vector(-0.22, -4.53) * mm, "endDerivative": vector(-0.33, -5.02) * mm});
            skLineSegment(sketch, "E104", {"start": v(-20.17, -26.6) * mm, "end": v(-18.99, -26.6) * mm});
            skLineSegment(sketch, "E105", {"start": v(-18.99, -26.6) * mm, "end": v(-19.42, -29.86) * mm});
            skLineSegment(sketch, "E106", {"start": v(-19.42, -29.86) * mm, "end": v(-16.9, -26.77) * mm});
            skLineSegment(sketch, "E107", {"start": v(-16.9, -26.77) * mm, "end": v(-15.83, -26.77) * mm});
            skLineSegment(sketch, "E108", {"start": v(-15.83, -26.77) * mm, "end": v(-16.03, -30.23) * mm});
            skLineSegment(sketch, "E109", {"start": v(-16.03, -30.23) * mm, "end": v(-12.88, -26.38) * mm});
            skLineSegment(sketch, "E110", {"start": v(-12.88, -26.38) * mm, "end": v(-11.39, -26.38) * mm});
            skLineSegment(sketch, "E111", {"start": v(-11.39, -26.38) * mm, "end": v(-16.05, -32.42) * mm});
            skLineSegment(sketch, "E112", {"start": v(-16.05, -32.42) * mm, "end": v(-16.84, -32.2) * mm});
            skLineSegment(sketch, "E113", {"start": v(-16.84, -32.2) * mm, "end": v(-17.63, -32.2) * mm});
            skLineSegment(sketch, "E114", {"start": v(-17.63, -32.2) * mm, "end": v(-17.23, -29.2) * mm});
            skLineSegment(sketch, "E115", {"start": v(-17.23, -29.2) * mm, "end": v(-19.88, -32.68) * mm});
            skLineSegment(sketch, "E116", {"start": v(-19.88, -32.68) * mm, "end": v(-20.5, -32.2) * mm});
            skLineSegment(sketch, "E117", {"start": v(-20.5, -32.2) * mm, "end": v(-20.93, -32.2) * mm});
            skLineSegment(sketch, "E118", {"start": v(-20.93, -32.2) * mm, "end": v(-20.17, -26.6) * mm});
            skSolve(sketch);
        }
        {
            var Q0;
            Q0=makeQuery(id+"F39.imprint","IMPRINT",FACE,{"disambiguationData":[TD([[makeQuery(id+"F39.imprint","IMPRINT",EDGE,{"derivedFrom":sQuery(id+"F39.wireOp",EDGE,"E88")}),1.0]])]});
            var sketch = newSketch(context, id + "F40", { "sketchPlane" : qUnion([Q0])});
            skText(sketch, "E119", { "text": "TOOL INC.", "fontName": "Tinos-Italic.ttf"});
            const initialGuessF40  = {"E119": [-0.00549, -0.028, 1, 0, 0.00228]};
            skSetInitialGuess(sketch, initialGuessF40);
            skSolve(sketch);
        }
        {
            var Q0;
            {var subQ3=sQuery(id+"F32.wireOp",EDGE,"E83");Q0=makeQuery(id+"F42.boolean.opBoolean","SPLIT",FACE,{"disambiguationData":[TD([makeQuery(id+"F38.boolean.opBoolean","COPY",FACE,{"derivedFrom":makeQuery(id+"F38.opExtrude","SWEPT_FACE",FACE,{"disambiguationData":[OSD([sQuery(id+"F37.wireOp",EDGE,"E87")])]})})])],"derivedFrom":makeQuery(id+"F33.opExtrude","SWEPT_FACE",FACE,{"disambiguationData":[OSD([subQ3])]})});}
            var sketch = newSketch(context, id + "F41", { "sketchPlane" : qUnion([Q0])});
            skText(sketch, "E120", { "text": "262-295-8670", "fontName": "OpenSans-Regular.ttf"});
            const initialGuessF41  = {"E120": [-0.00465, -0.03603, 1, 0, 0.00292]};
            skSetInitialGuess(sketch, initialGuessF41);
            skSolve(sketch);
        }
        {
            var Q0;
            Q0=makeQuery(id+"F39.imprint","IMPRINT",FACE,{"disambiguationData":[TD([[makeQuery(id+"F39.imprint","IMPRINT",EDGE,{"derivedFrom":sQuery(id+"F39.wireOp",EDGE,"E88")}),-1.0]])]});
            var Q1;
            Q1=makeQuery(id+"F39.imprint","IMPRINT",FACE,{"disambiguationData":[TD([[makeQuery(id+"F39.imprint","IMPRINT",EDGE,{"derivedFrom":sQuery(id+"F39.wireOp",EDGE,"E104")}),-1.0]])]});
            var Q2;
            Q2 = qSketchRegion(id + "F40", true);
            var Q3;
            Q3 = qSketchRegion(id + "F41", true);
            extrude(context, id + "F42", {"entities" : qUnion([Q0, Q1, Q2, Q3]), "operationType" : NewBodyOperationType.REMOVE, "oppositeDirection" : true, "depth" : 0.25 * mm, "offsetDistance" : 25.4 * mm});
        }
        {
            var Q0;
            Q0=makeQuery(id+"F36.boolean.opBoolean","INTERSECT",EDGE,{"derivedFrom":[makeQuery(id+"F34.boolean.opBoolean","COPY",FACE,{"derivedFrom":makeQuery(id+"F34.opExtrude","SWEPT_FACE",FACE,{"disambiguationData":[OSD([sQuery(id+"F32.wireOp",EDGE,"E63")])]})}),makeQuery(id+"F36.opExtrude","SWEPT_FACE",FACE,{"disambiguationData":[OSD([sQuery(id+"F35.wireOp",EDGE,"E85")])]})]});
            var Q1;
            Q1=makeQuery(id+"F36.boolean.opBoolean","COPY",EDGE,{"derivedFrom":makeQuery(id+"F36.opExtrude","SWEPT_EDGE",EDGE,{"disambiguationData":[OSD([sQuery(id+"F32.wireOp",EDGE,"E62.top"),sQuery(id+"F32.wireOp",EDGE,"E80"),sQuery(id+"F35.wireOp",EDGE,"E85")])]})});
            var Q2;
            Q2=makeQuery(id+"F36.boolean.opBoolean","COPY",EDGE,{"derivedFrom":makeQuery(id+"F36.opExtrude","CAP_EDGE",EDGE,{"disambiguationData":[OSD([sQuery(id+"F35.wireOp",EDGE,"E85")])],"isStart":true})});
            var Q3;
            {var subQ0=sQuery(id+"F32.wireOp",EDGE,"E62.right");Q3=makeQuery(id+"F36.boolean.opBoolean","MERGE",EDGE,{"derivedFrom":[makeQuery(id+"F33.opExtrude","CAP_EDGE",EDGE,{"disambiguationData":[OSD([subQ0,sQuery(id+"F32.wireOp",EDGE,"E82")])],"isStart":true}),makeQuery(id+"F36.opExtrude","SWEPT_EDGE",EDGE,{"disambiguationData":[OSD([sQuery(id+"F32.wireOp",EDGE,"E62.top"),subQ0,sQuery(id+"F35.wireOp",EDGE,"E85")])]})]});}
            var Q4;
            Q4=makeQuery(id+"F34.boolean.opBoolean","COPY",EDGE,{"derivedFrom":makeQuery(id+"F34.opExtrude","SWEPT_EDGE",EDGE,{"disambiguationData":[OSD([sQuery(id+"F32.wireOp",EDGE,"E62.right"),sQuery(id+"F32.wireOp",EDGE,"E63")])]})});
            var Q5;
            {var subQ0=sQuery(id+"F32.wireOp",EDGE,"E82");Q5=makeQuery(id+"F38.boolean.opBoolean","MERGE",EDGE,{"derivedFrom":[makeQuery(id+"F34.boolean.opBoolean","COPY",EDGE,{"derivedFrom":makeQuery(id+"F34.opExtrude","CAP_EDGE",EDGE,{"disambiguationData":[OSD([sQuery(id+"F32.wireOp",EDGE,"E62.right"),subQ0])],"isStart":false})}),makeQuery(id+"F38.opExtrude","SWEPT_EDGE",EDGE,{"disambiguationData":[OSD([subQ0,sQuery(id+"F32.wireOp",EDGE,"E83"),sQuery(id+"F37.wireOp",EDGE,"E87")])]})]});}
            var Q6;
            {var subQ0=sQuery(id+"F32.wireOp",EDGE,"E83");var subQ1=makeQuery(id+"F33.opExtrude","SWEPT_EDGE",EDGE,{"disambiguationData":[OSD([subQ0,sQuery(id+"F32.wireOp",EDGE,"E84")])]});Q6=makeQuery(id+"F38.boolean.opBoolean","COPY",EDGE,{"derivedFrom":makeQuery(id+"F38.opExtrude","TWEAK_EDGE",EDGE,{"derivedFrom":[makeQuery(id+"F34.boolean.opBoolean","COPY",FACE,{"derivedFrom":makeQuery(id+"F34.opExtrude","SWEPT_FACE",FACE,{"disambiguationData":[OSD([sQuery(id+"F32.wireOp",EDGE,"E63")])]})}),makeQuery(id+"F37.imprint","IMPRINT",EDGE,{"disambiguationData":[TD([[makeQuery(id+"F37.imprint","INTERSECT",VERTEX,{"derivedFrom":[makeQuery(id+"F34.boolean.opBoolean","COPY",EDGE,{"derivedFrom":makeQuery(id+"F34.opExtrude","CAP_EDGE",EDGE,{"disambiguationData":[OSD([subQ0])],"isStart":false})}),subQ1]}),1.0]])],"derivedFrom":subQ1})]})});}
            var Q7;
            Q7=makeQuery(id+"F38.boolean.opBoolean","COPY",EDGE,{"derivedFrom":makeQuery(id+"F38.opExtrude","SWEPT_EDGE",EDGE,{"disambiguationData":[OSD([sQuery(id+"F32.wireOp",EDGE,"E83"),sQuery(id+"F32.wireOp",EDGE,"E84"),sQuery(id+"F37.wireOp",EDGE,"E87")])]})});
            var Q8;
            Q8=makeQuery(id+"F38.boolean.opBoolean","COPY",EDGE,{"derivedFrom":makeQuery(id+"F38.opExtrude","CAP_EDGE",EDGE,{"disambiguationData":[OSD([sQuery(id+"F37.wireOp",EDGE,"E87")])],"isStart":true})});
            var Q9;
            Q9=makeQuery(id+"F33.opExtrude","SWEPT_EDGE",EDGE,{"disambiguationData":[OSD([sQuery(id+"F32.wireOp",EDGE,"E62.top"),sQuery(id+"F32.wireOp",EDGE,"E80")])]});
            var Q10;
            Q10=makeQuery(id+"F33.opExtrude","SWEPT_EDGE",EDGE,{"disambiguationData":[OSD([sQuery(id+"F32.wireOp",EDGE,"E62.top"),sQuery(id+"F32.wireOp",EDGE,"E62.right")])]});
            var Q11;
            Q11=makeQuery(id+"F33.opExtrude","CAP_EDGE",EDGE,{"disambiguationData":[OSD([sQuery(id+"F32.wireOp",EDGE,"E62.right"),sQuery(id+"F32.wireOp",EDGE,"E82")])],"isStart":false});
            var Q12;
            Q12=makeQuery(id+"F33.opExtrude","SWEPT_EDGE",EDGE,{"disambiguationData":[OSD([sQuery(id+"F32.wireOp",EDGE,"E82"),sQuery(id+"F32.wireOp",EDGE,"E83")])]});
            var Q13;
            Q13=makeQuery(id+"F33.opExtrude","SWEPT_EDGE",EDGE,{"disambiguationData":[OSD([sQuery(id+"F32.wireOp",EDGE,"E83"),sQuery(id+"F32.wireOp",EDGE,"E84")])]});
            var Q14;
            Q14=makeQuery(id+"F33.opExtrude","CAP_EDGE",EDGE,{"disambiguationData":[OSD([sQuery(id+"F32.wireOp",EDGE,"E80"),sQuery(id+"F32.wireOp",EDGE,"E84")])],"isStart":false});
            var Q15;
            Q15=makeQuery(id+"F33.opExtrude","CAP_EDGE",EDGE,{"disambiguationData":[OSD([sQuery(id+"F32.wireOp",EDGE,"E62.top")])],"isStart":false});
            var Q16;
            Q16=makeQuery(id+"F33.opExtrude","CAP_EDGE",EDGE,{"disambiguationData":[OSD([sQuery(id+"F32.wireOp",EDGE,"E83")])],"isStart":false});
            chamfer(context, id + "F43", {"entities" : qUnion([Q0, Q1, Q2, Q3, Q4, Q5, Q6, Q7, Q8, Q9, Q10, Q11, Q12, Q13, Q14, Q15, Q16]), "width" : 0.32 * mm, "tangentPropagation" : true});
        }
    });
